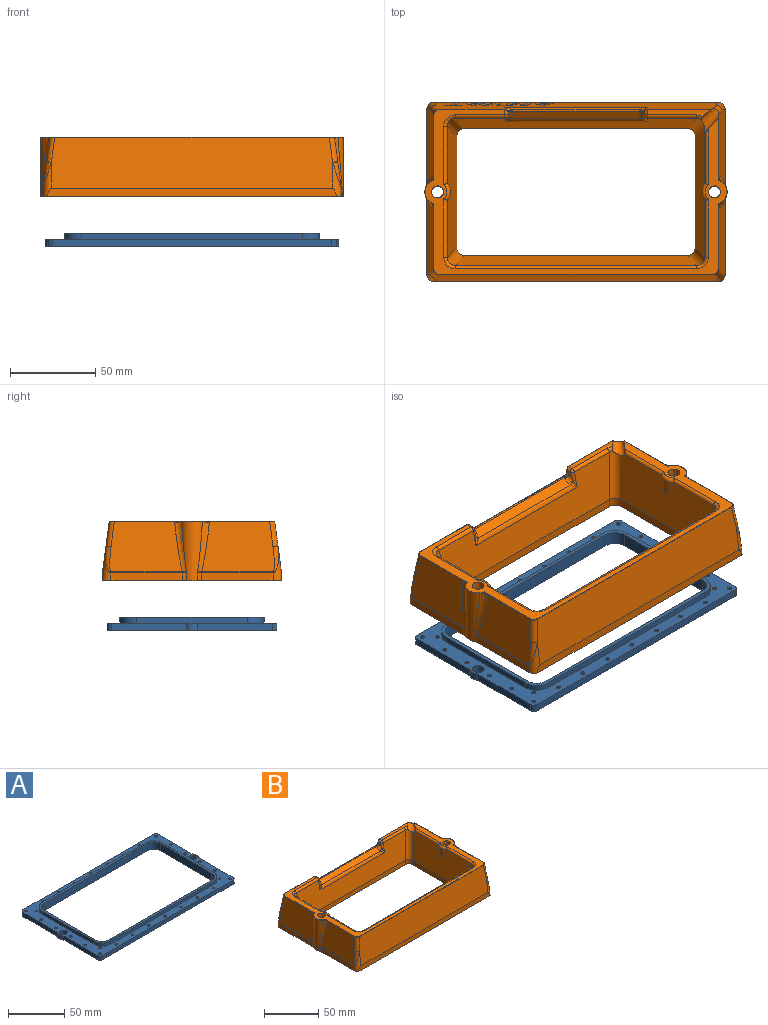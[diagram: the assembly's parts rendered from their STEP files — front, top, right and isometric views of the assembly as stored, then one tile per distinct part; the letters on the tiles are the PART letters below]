
ASSEMBLY  parts=2 mates=1
PART A: 104 faces, bbox 172.1x99.6x8 mm
  f0: plane 172.1x99.6mm, normal (0,0,-1), area 4703.2mm2, adj f3,f4,f5,f6,f7,f8,f9,f10
  f1: plane 172.1x99.6mm, normal (0,0,1), area 4007.9mm2, adj f3,f4,f5,f6,f7,f8,f9,f10
  f2: plane 149.6x84.6mm, normal (0,0,1), area 934.5mm2, adj f17,f18,f19,f20,f21,f22,f23,f24
  f3: plane 43.77x4.5mm, normal (1,0,0), area 197mm2, adj f0,f1,f4,f16
  f4: cylinder r=2.8mm len=4.5mm, axis (0,0,-1), area 19.8mm2, adj f0,f1,f3,f5
  f5: plane 164x4.5mm, normal (0,-1,0), area 738mm2, adj f0,f1,f4,f6
  f6: cylinder r=2.8mm len=4.5mm, axis (0,0,-1), area 19.8mm2, adj f0,f1,f5,f7
  f7: plane 43.77x4.5mm, normal (-1,0,0), area 197mm2, adj f0,f1,f6,f8
  f8: cylinder r=4.8mm len=6.46mm, axis (0,0,-1), area 31.9mm2, adj f0,f1,f7,f9
  f9: plane 43.77x4.5mm, normal (-1,0,0), area 197mm2, adj f0,f1,f8,f10
  f10: cylinder r=2.8mm len=4.5mm, axis (0,0,-1), area 19.8mm2, adj f0,f1,f9,f11
  f11: plane 164x4.5mm, normal (0,1,0), area 738mm2, adj f0,f1,f10,f12
  f12: cylinder r=2.8mm len=4.5mm, axis (0,0,-1), area 19.8mm2, adj f0,f1,f11,f13
  f13: plane 43.77x4.5mm, normal (1,0,0), area 197mm2, adj f0,f1,f12,f16
  f14: extruded ~6.97x6.97mm, area 99mm2, adj f0,f1
  f15: cylinder r=3.5mm len=7mm, axis (0,0,-1), area 99mm2, adj f0,f1
  f16: cylinder r=4.8mm len=6.46mm, axis (0,0,-1), area 31.9mm2, adj f0,f1,f3,f13
  f17: cylinder r=7.7mm len=8mm, axis (0,0,-1), area 96.8mm2, adj f0,f2,f18,f24
  f18: plane 65x8mm, normal (1,0,0), area 520mm2, adj f0,f2,f17,f19
  f19: cylinder r=7.7mm len=8mm, axis (0,0,-1), area 96.8mm2, adj f0,f2,f18,f20
  f20: plane 130x8mm, normal (0,-1,0), area 1040mm2, adj f0,f2,f19,f21
  f21: cylinder r=7.7mm len=8mm, axis (0,0,-1), area 96.8mm2, adj f0,f2,f20,f22
  f22: plane 65x8mm, normal (-1,0,0), area 520mm2, adj f0,f2,f21,f23
  f23: cylinder r=7.7mm len=8mm, axis (0,0,-1), area 96.8mm2, adj f0,f2,f22,f24
  f24: plane 130x8mm, normal (0,1,0), area 1040mm2, adj f0,f2,f17,f23
  f25: plane 65x0.5mm, normal (1,0,0), area 32.5mm2, adj f1,f26,f32,f41
  f26: cylinder r=10mm len=10mm, axis (0,0,1), area 7.9mm2, adj f1,f25,f27,f41
  f27: plane 130x0.5mm, normal (0,1,0), area 65mm2, adj f1,f26,f28,f41
  f28: cylinder r=10mm len=10mm, axis (0,0,1), area 7.9mm2, adj f1,f27,f29,f41
  f29: plane 65x0.5mm, normal (-1,0,0), area 32.5mm2, adj f1,f28,f30,f41
  f30: cylinder r=10mm len=10mm, axis (0,0,1), area 7.9mm2, adj f1,f29,f31,f41
  f31: plane 130x0.5mm, normal (0,-1,0), area 65mm2, adj f1,f30,f32,f41
  f32: cylinder r=10mm len=10mm, axis (0,0,1), area 7.9mm2, adj f1,f25,f31,f41
  f33: plane 65x4mm, normal (-1,0,0), area 260mm2, adj f2,f34,f40,f41
  f34: cylinder r=9.8mm len=9.8mm, axis (0,0,1), area 61.6mm2, adj f2,f33,f35,f41
  f35: plane 130x4mm, normal (0,1,0), area 520mm2, adj f2,f34,f36,f41
  f36: cylinder r=9.8mm len=9.8mm, axis (0,0,1), area 61.6mm2, adj f2,f35,f37,f41
  f37: plane 65x4mm, normal (1,0,0), area 260mm2, adj f2,f36,f38,f41
  f38: cylinder r=9.8mm len=9.8mm, axis (0,0,1), area 61.6mm2, adj f2,f37,f39,f41
  f39: plane 130x4mm, normal (0,-1,0), area 520mm2, adj f2,f38,f40,f41
  f40: cylinder r=9.8mm len=9.8mm, axis (0,0,1), area 61.6mm2, adj f2,f33,f39,f41
  f41: plane 150x85mm, normal (0,0,1), area 90.4mm2, adj f25,f26,f27,f28,f29,f30,f31,f32
  f42: cylinder r=1.25mm len=3.5mm, axis (0,0,-1), area 27.5mm2, adj f1,f91
  f43: cylinder r=1.25mm len=3.5mm, axis (0,0,-1), area 27.5mm2, adj f1,f77
  f44: cylinder r=1.25mm len=3.5mm, axis (0,0,-1), area 27.5mm2, adj f1,f75
  f45: cylinder r=1.25mm len=3.5mm, axis (0,0,-1), area 27.5mm2, adj f1,f74
  f46: cylinder r=1.25mm len=3.5mm, axis (0,0,-1), area 27.5mm2, adj f1,f73
  f47: cylinder r=1.25mm len=3.5mm, axis (0,0,-1), area 27.5mm2, adj f1,f89
  f48: cylinder r=1.25mm len=3.5mm, axis (0,0,-1), area 27.5mm2, adj f1,f88
  f49: cylinder r=1.25mm len=3.5mm, axis (0,0,-1), area 27.5mm2, adj f1,f87
  f50: cylinder r=1.25mm len=3.5mm, axis (0,0,-1), area 27.5mm2, adj f1,f102
  f51: cylinder r=1.25mm len=3.5mm, axis (0,0,-1), area 27.5mm2, adj f1,f76
  f52: cylinder r=1.25mm len=3.5mm, axis (0,0,-1), area 27.5mm2, adj f1,f86
  f53: cylinder r=1.25mm len=3.5mm, axis (0,0,-1), area 27.5mm2, adj f1,f92
  f54: cylinder r=1.25mm len=3.5mm, axis (0,0,-1), area 27.5mm2, adj f1,f103
  f55: cylinder r=1.25mm len=3.5mm, axis (0,0,-1), area 13.8mm2, adj f1,f56,f101
  f56: cylinder r=1.25mm len=3.5mm, axis (0,0,-1), area 13.8mm2, adj f1,f55,f100
  f57: cylinder r=1.25mm len=3.5mm, axis (0,0,-1), area 27.5mm2, adj f1,f83
  f58: cylinder r=1.25mm len=3.5mm, axis (0,0,-1), area 27.5mm2, adj f1,f95
  f59: cylinder r=1.25mm len=3.5mm, axis (0,0,-1), area 27.5mm2, adj f1,f82
  f60: cylinder r=1.25mm len=3.5mm, axis (0,0,-1), area 27.5mm2, adj f1,f96
  f61: cylinder r=1.25mm len=3.5mm, axis (0,0,-1), area 27.5mm2, adj f1,f85
  f62: cylinder r=1.25mm len=3.5mm, axis (0,0,-1), area 27.5mm2, adj f1,f93
  f63: cylinder r=1.25mm len=3.5mm, axis (0,0,-1), area 27.5mm2, adj f1,f84
  f64: cylinder r=1.25mm len=3.5mm, axis (0,0,-1), area 27.5mm2, adj f1,f94
  f65: cylinder r=1.25mm len=3.5mm, axis (0,0,-1), area 27.5mm2, adj f1,f79
  f66: cylinder r=1.25mm len=3.5mm, axis (0,0,-1), area 27.5mm2, adj f1,f99
  f67: cylinder r=1.25mm len=3.5mm, axis (0,0,-1), area 27.5mm2, adj f1,f78
  f68: cylinder r=1.25mm len=3.5mm, axis (0,0,-1), area 27.5mm2, adj f1,f90
  f69: cylinder r=1.25mm len=3.5mm, axis (0,0,-1), area 27.5mm2, adj f1,f81
  f70: cylinder r=1.25mm len=3.5mm, axis (0,0,-1), area 27.5mm2, adj f1,f97
  f71: cylinder r=1.25mm len=3.5mm, axis (0,0,-1), area 27.5mm2, adj f1,f80
  f72: cylinder r=1.25mm len=3.5mm, axis (0,0,-1), area 27.5mm2, adj f1,f98
  f73: cone r=1.25mm half-angle=45deg, axis (0,0,-1), area 15.6mm2, adj f0,f46
  f74: cone r=1.25mm half-angle=45deg, axis (0,0,-1), area 15.6mm2, adj f0,f45
  f75: cone r=1.25mm half-angle=45deg, axis (0,0,-1), area 15.6mm2, adj f0,f44
  f76: cone r=1.25mm half-angle=45deg, axis (0,0,-1), area 15.6mm2, adj f0,f51
  f77: cone r=1.25mm half-angle=45deg, axis (0,0,-1), area 15.6mm2, adj f0,f43
  f78: cone r=1.25mm half-angle=45deg, axis (0,0,-1), area 15.6mm2, adj f0,f67
  f79: cone r=1.25mm half-angle=45deg, axis (0,0,-1), area 15.6mm2, adj f0,f65
  f80: cone r=1.25mm half-angle=45deg, axis (0,0,-1), area 15.6mm2, adj f0,f71
  f81: cone r=1.25mm half-angle=45deg, axis (0,0,-1), area 15.6mm2, adj f0,f69
  f82: cone r=1.25mm half-angle=45deg, axis (0,0,-1), area 15.6mm2, adj f0,f59
  f83: cone r=1.25mm half-angle=45deg, axis (0,0,-1), area 15.6mm2, adj f0,f57
  f84: cone r=1.25mm half-angle=45deg, axis (0,0,-1), area 15.6mm2, adj f0,f63
  f85: cone r=1.25mm half-angle=45deg, axis (0,0,-1), area 15.6mm2, adj f0,f61
  f86: cone r=2.25mm half-angle=45deg, axis (0,0,-1), area 15.6mm2, adj f0,f52
  f87: cone r=1.25mm half-angle=45deg, axis (0,0,-1), area 15.6mm2, adj f0,f49
  f88: cone r=1.25mm half-angle=45deg, axis (0,0,-1), area 15.6mm2, adj f0,f48
  f89: cone r=1.25mm half-angle=45deg, axis (0,0,-1), area 15.6mm2, adj f0,f47
  f90: cone r=1.25mm half-angle=45deg, axis (0,0,-1), area 15.6mm2, adj f0,f68
  f91: cone r=1.25mm half-angle=45deg, axis (0,0,-1), area 15.6mm2, adj f0,f42
  f92: cone r=1.25mm half-angle=45deg, axis (0,0,-1), area 15.6mm2, adj f0,f53
  f93: cone r=1.25mm half-angle=45deg, axis (0,0,-1), area 15.6mm2, adj f0,f62
  f94: cone r=1.25mm half-angle=45deg, axis (0,0,-1), area 15.6mm2, adj f0,f64
  f95: cone r=1.25mm half-angle=45deg, axis (0,0,-1), area 15.6mm2, adj f0,f58
  f96: cone r=1.25mm half-angle=45deg, axis (0,0,-1), area 15.6mm2, adj f0,f60
  f97: cone r=1.25mm half-angle=45deg, axis (0,0,-1), area 15.6mm2, adj f0,f70
  f98: cone r=1.25mm half-angle=45deg, axis (0,0,-1), area 15.6mm2, adj f0,f72
  f99: cone r=1.25mm half-angle=45deg, axis (0,0,-1), area 15.6mm2, adj f0,f66
  f100: cone r=1.25mm half-angle=45deg, axis (0,0,-1), area 7.8mm2, adj f0,f56,f101
  f101: cone r=1.25mm half-angle=45deg, axis (0,0,-1), area 7.8mm2, adj f0,f55,f100
  f102: cone r=1.25mm half-angle=45deg, axis (0,0,-1), area 15.6mm2, adj f0,f50
  f103: cone r=2.25mm half-angle=45deg, axis (0,0,-1), area 15.6mm2, adj f0,f54
PART B: 310 faces, bbox 180.4x108x38.9 mm
  f0: plane 36.86x4.25mm, normal (0,0,1), area 113.1mm2, adj f1,f306,f307,f308,f309
  f1: bspline ~3.52x2.61mm, area 7.5mm2, adj f0,f2,f306,f309
  f2: cylinder r=5mm len=29.23mm, axis (0.19,0.19,0.96), area 222.6mm2, adj f1,f3,f304,f305,f309
  f3: plane 76.19x28.42mm, normal (-0.98,0,0.2), area 1980mm2, adj f2,f4,f298,f299,f300,f301,f302,f303
  f4: cylinder r=2mm len=32.81mm, axis (0,-1,0), area 86.4mm2, adj f3,f5,f299,f309
  f5: plane 177.35x96.9mm, normal (0,0,1), area 1738mm2, adj f4,f6,f268,f269,f270,f271,f272,f273
  f6: cylinder r=3.5mm len=30mm, axis (0,0,-1), area 659.7mm2, adj f5,f7
  f7: plane 172.5x100mm, normal (0,0,-1), area 4115.4mm2, adj f6,f8,f10,f12,f172,f173,f174,f175
  f8: cylinder r=1.25mm len=5mm, axis (0,0,-1), area 39.3mm2, adj f7,f9
  f9: plane 2.5x2.5mm, normal (0,0,-1), area 4.9mm2, adj f8
  f10: cylinder r=1.25mm len=5mm, axis (0,0,-1), area 39.3mm2, adj f7,f11
  f11: plane 2.5x2.5mm, normal (0,0,-1), area 4.9mm2, adj f10
  f12: cylinder r=5mm len=6.61mm, axis (0,0,-1), area 36.1mm2, adj f7,f13,f172,f182
  f13: plane 177.59x105.09mm, normal (0,0,-1), area 1373.2mm2, adj f12,f14,f36,f158,f159,f160,f161,f162
  f14: cylinder r=5mm len=4.67mm, axis (0,0,1), area 10.5mm2, adj f13,f15,f36,f171
  f15: bspline ~2.65x2.48mm, area 2.3mm2, adj f14,f16,f35,f36
  f16: bspline ~29.47x6.76mm, area 107.7mm2, adj f15,f17,f20,f36
  f17: bspline ~4.16x2.62mm, area 1.6mm2, adj f16,f18,f20,f273
  f18: bspline ~4.04x2.27mm, area 2.2mm2, adj f17,f19,f273,f276
  f19: bspline ~0.63x0.47mm, area 0mm2, adj f18,f274,f275
  f20: plane 44.36x31.16mm, normal (0.99,0,0.13), area 1161mm2, adj f16,f17,f21,f23,f35,f276
  f21: bspline ~15.36x4.97mm, area 46.2mm2, adj f20,f22,f23,f170
  f22: bspline ~1.14x1.07mm, area 0.1mm2, adj f21,f35,f170
  f23: cylinder r=3mm len=14.79mm, axis (0.13,-0.13,-0.98), area 69.4mm2, adj f20,f21,f24,f277
  f24: plane 165x29.83mm, normal (0,-0.99,0.13), area 4936.1mm2, adj f23,f25,f168,f169,f170,f278
  f25: cylinder r=3mm len=14.79mm, axis (-0.13,-0.13,-0.98), area 69.4mm2, adj f24,f26,f34,f279
  f26: bspline ~15.36x4.97mm, area 46.2mm2, adj f25,f27,f34,f168
  f27: bspline ~1.14x1.07mm, area 0.1mm2, adj f26,f28,f168
  f28: cylinder r=5mm len=42.28mm, axis (0,-1,0), area 27.9mm2, adj f27,f29,f34,f167
  f29: bspline ~2.48x2.36mm, area 2.3mm2, adj f28,f30,f165,f166
  f30: bspline ~29.47x6.76mm, area 107.7mm2, adj f29,f31,f34,f165
  f31: bspline ~4.16x2.62mm, area 1.6mm2, adj f30,f32,f34,f283
  f32: bspline ~4.04x2.27mm, area 2.2mm2, adj f31,f33,f280,f283
  f33: bspline ~0.63x0.47mm, area 0mm2, adj f32,f281,f282
  f34: plane 44.36x31.16mm, normal (-0.99,0,0.13), area 1161mm2, adj f25,f26,f28,f30,f31,f280
  f35: cylinder r=5mm len=42.28mm, axis (0,1,0), area 27.9mm2, adj f15,f20,f22,f171
  f36: cylinder r=7.5mm len=34.8mm, axis (0,0,1), area 355.5mm2, adj f13,f14,f15,f16,f37,f157,f158,f273
  f37: bspline ~29.47x6.76mm, area 107.7mm2, adj f36,f38,f154,f157
  f38: plane 44.36x31.16mm, normal (0.99,0,0.13), area 1159.1mm2, adj f37,f39,f151,f153,f154,f270,f309
  f39: cylinder r=3mm len=13.4mm, axis (-0.13,-0.13,0.98), area 62.3mm2, adj f38,f40,f151,f309
  f40: plane 165.16x29.99mm, normal (0,0.99,0.13), area 3946.1mm2, adj f39,f41,f50,f51,f52,f53,f54,f55
  f41: plane 2.79x0.99mm, normal (0,-0.13,0.99), area 2.8mm2, adj f40,f42,f50,f56
  f42: plane 13.68x12.08mm, normal (0,0.99,0.13), area 81.1mm2, adj f41,f43,f45,f46,f47,f48,f49,f50
  f43: extruded ~2.49x1.31mm, area 2.4mm2, adj f42,f44,f45,f49
  f44: plane 5.95x3.13mm, normal (0,0.99,0.13), area 8.9mm2, adj f43,f45,f46,f47,f48,f49
  f45: plane 1.04x0.47mm, normal (-1,0,0), area 0.3mm2, adj f42,f43,f44,f46
  f46: extruded ~2.5x1.31mm, area 2.6mm2, adj f42,f44,f45,f47
  f47: plane 3.72x1.77mm, normal (0.9,-0.06,0.43), area 4mm2, adj f42,f44,f46,f48
  f48: plane 3.13x0.99mm, normal (0,0.13,-0.99), area 3.1mm2, adj f42,f44,f47,f49
  f49: plane 3.39x1.43mm, normal (-1,-0.01,0.07), area 3.3mm2, adj f42,f43,f44,f48
  f50: plane 13.81x2.81mm, normal (1,0.01,-0.1), area 13.9mm2, adj f40,f41,f42,f51
  f51: plane 3.51x0.99mm, normal (0,0.13,-0.99), area 3.5mm2, adj f40,f42,f50,f52
  f52: plane 13.81x7.2mm, normal (-0.89,0.06,-0.46), area 15.6mm2, adj f40,f42,f51,f53
  f53: plane 3.01x0.99mm, normal (0,-0.13,0.99), area 3mm2, adj f40,f42,f52,f54
  f54: plane 3.38x1.62mm, normal (0.9,-0.06,0.44), area 3.6mm2, adj f40,f42,f53,f55
  f55: plane 4.44x0.99mm, normal (0,-0.13,0.99), area 4.4mm2, adj f40,f42,f54,f56
  f56: plane 3.38x1.42mm, normal (-1,-0.01,0.07), area 3.3mm2, adj f40,f41,f42,f55
  f57: extruded ~1.53x1.18mm, area 1.4mm2, adj f40,f58,f59,f68
  f58: plane 13.62x11.36mm, normal (0,0.99,0.13), area 70.5mm2, adj f57,f59,f60,f61,f62,f63,f64,f65
  f59: extruded ~1.37x1.16mm, area 1.3mm2, adj f40,f57,f58,f60
  f60: plane 8.33x2.08mm, normal (1,0.01,-0.06), area 8.3mm2, adj f40,f58,f59,f61
  f61: plane 2.77x0.99mm, normal (0,0.13,-0.99), area 2.8mm2, adj f40,f58,f60,f62
  f62: plane 13.75x2.81mm, normal (-1,-0.01,0.09), area 13.8mm2, adj f40,f58,f61,f63
  f63: plane 3.14x0.99mm, normal (0,-0.13,0.99), area 3.1mm2, adj f40,f58,f62,f64
  f64: plane 13.75x7.03mm, normal (0.89,-0.06,0.45), area 15.4mm2, adj f40,f58,f63,f65
  f65: plane 2.97x0.99mm, normal (0,0.13,-0.99), area 3mm2, adj f40,f58,f64,f66
  f66: plane 8.33x4.06mm, normal (-0.9,0.06,-0.44), area 9.2mm2, adj f40,f58,f65,f67
  f67: extruded ~2.77x1.34mm, area 2.9mm2, adj f40,f58,f66,f68
  f68: plane 0.99x0.13mm, normal (0,0.13,-0.99), area 0.1mm2, adj f40,f57,f58,f67
  f69: plane 10.31x2.35mm, normal (1,0.01,-0.06), area 10.3mm2, adj f40,f70,f71,f87
  f70: plane 16.53x13.62mm, normal (0,0.99,0.13), area 126.7mm2, adj f69,f71,f72,f73,f74,f75,f76,f77
  f71: plane 3.8x0.99mm, normal (0,0.13,-0.99), area 3.8mm2, adj f40,f69,f70,f72
  f72: plane 13.75x2.9mm, normal (-0.98,0.03,-0.2), area 14mm2, adj f40,f70,f71,f73
  f73: plane 2.58x0.99mm, normal (0,-0.13,0.99), area 2.6mm2, adj f40,f70,f72,f74
  f74: extruded ~8.54x2.11mm, area 8.7mm2, adj f40,f70,f73,f75
  f75: extruded ~2.28x1.28mm, area 2.2mm2, adj f40,f70,f74,f76
  f76: plane 0.99x0.13mm, normal (0,-0.13,0.99), area 0mm2, adj f40,f70,f75,f77
  f77: plane 10.69x2.4mm, normal (-1,-0.01,0.05), area 10.7mm2, adj f40,f70,f76,f78
  f78: plane 2.64x0.99mm, normal (0,-0.13,0.99), area 2.6mm2, adj f40,f70,f77,f79
  f79: plane 10.69x5.35mm, normal (0.89,-0.06,0.44), area 11.9mm2, adj f40,f70,f78,f80
  f80: plane 0.99x0.13mm, normal (0,-0.13,0.99), area 0mm2, adj f40,f70,f79,f81
  f81: extruded ~4.24x1.54mm, area 4.3mm2, adj f40,f70,f80,f82
  f82: plane 6.58x1.85mm, normal (-0.98,0.03,-0.2), area 6.6mm2, adj f40,f70,f81,f83
  f83: plane 2.63x0.99mm, normal (0,-0.13,0.99), area 2.6mm2, adj f40,f70,f82,f84
  f84: plane 13.75x2.91mm, normal (0.98,-0.03,0.21), area 14mm2, adj f40,f70,f83,f85
  f85: plane 3.98x0.99mm, normal (0,0.13,-0.99), area 4mm2, adj f40,f70,f84,f86
  f86: plane 10.31x5.18mm, normal (-0.89,0.06,-0.45), area 11.5mm2, adj f40,f70,f85,f87
  f87: plane 0.99x0.13mm, normal (0,0.13,-0.99), area 0mm2, adj f40,f69,f70,f86
  f88: plane 2.79x0.99mm, normal (0,-0.13,0.99), area 2.8mm2, adj f40,f89,f97,f103
  f89: plane 13.68x12.08mm, normal (0,0.99,0.13), area 81.1mm2, adj f88,f90,f92,f93,f94,f95,f96,f97
  f90: extruded ~2.49x1.31mm, area 2.4mm2, adj f89,f91,f92,f96
  f91: plane 5.95x3.13mm, normal (0,0.99,0.13), area 8.9mm2, adj f90,f92,f93,f94,f95,f96
  f92: plane 1.04x0.47mm, normal (-1,0,0), area 0.3mm2, adj f89,f90,f91,f93
  f93: extruded ~2.5x1.31mm, area 2.6mm2, adj f89,f91,f92,f94
  f94: plane 3.72x1.77mm, normal (0.9,-0.06,0.43), area 4mm2, adj f89,f91,f93,f95
  f95: plane 3.13x0.99mm, normal (0,0.13,-0.99), area 3.1mm2, adj f89,f91,f94,f96
  f96: plane 3.39x1.43mm, normal (-1,-0.01,0.07), area 3.3mm2, adj f89,f90,f91,f95
  f97: plane 13.81x2.81mm, normal (1,0.01,-0.1), area 13.9mm2, adj f40,f88,f89,f98
  f98: plane 3.51x0.99mm, normal (0,0.13,-0.99), area 3.5mm2, adj f40,f89,f97,f99
  f99: plane 13.81x7.2mm, normal (-0.89,0.06,-0.46), area 15.6mm2, adj f40,f89,f98,f100
  f100: plane 3.01x0.99mm, normal (0,-0.13,0.99), area 3mm2, adj f40,f89,f99,f101
  f101: plane 3.38x1.62mm, normal (0.9,-0.06,0.44), area 3.6mm2, adj f40,f89,f100,f102
  f102: plane 4.44x0.99mm, normal (0,-0.13,0.99), area 4.4mm2, adj f40,f89,f101,f103
  f103: plane 3.38x1.42mm, normal (-1,-0.01,0.07), area 3.3mm2, adj f40,f88,f89,f102
  f104: plane 3.32x0.99mm, normal (0,-0.13,0.99), area 3.3mm2, adj f40,f105,f106,f112
  f105: plane 13.62x10.01mm, normal (0,0.99,0.13), area 55.4mm2, adj f104,f106,f107,f108,f109,f110,f111,f112
  f106: plane 2.53x1.31mm, normal (0.98,-0.03,0.21), area 2.5mm2, adj f40,f104,f105,f107
  f107: plane 9.49x0.99mm, normal (0,0.13,-0.99), area 9.5mm2, adj f40,f105,f106,f108
  f108: plane 2.53x1.31mm, normal (-0.98,0.03,-0.21), area 2.5mm2, adj f40,f105,f107,f109
  f109: plane 3.31x0.99mm, normal (0,-0.13,0.99), area 3.3mm2, adj f40,f105,f108,f110
  f110: plane 11.35x2.49mm, normal (-0.98,0.03,-0.2), area 11.6mm2, adj f40,f105,f109,f111
  f111: plane 2.87x0.99mm, normal (0,-0.13,0.99), area 2.9mm2, adj f40,f105,f110,f112
  f112: plane 11.35x2.49mm, normal (0.98,-0.03,0.2), area 11.6mm2, adj f40,f104,f105,f111
  f113: cylinder r=2mm len=6.83mm, axis (0,-0.13,0.99), area 9.1mm2, adj f40,f114,f115,f134,f135,f136
  f114: bspline ~2.28x2mm, area 0.4mm2, adj f113,f307,f308
  f115: plane 1.89x1.26mm, normal (-1,0,0), area 1mm2, adj f113,f116,f132,f133,f307
  f116: cylinder r=2mm len=10.44mm, axis (0,0.2,0.98), area 18mm2, adj f115,f117,f118,f131,f304
  f117: sphere r=2mm, area 5.7mm2, adj f116,f306,f307
  f118: bspline ~5.1x4.05mm, area 5.1mm2, adj f116,f119,f131
  f119: cylinder r=5mm len=84mm, axis (1,0,0), area 275.2mm2, adj f118,f120,f130,f304
  f120: bspline ~5.1x4.05mm, area 5.1mm2, adj f119,f121,f129
  f121: cylinder r=2mm len=10.44mm, axis (0,-0.2,-0.98), area 18mm2, adj f120,f122,f123,f129,f304
  f122: sphere r=2mm, area 7.8mm2, adj f121,f289,f290
  f123: plane 1.89x1.26mm, normal (1,0,0), area 1mm2, adj f121,f124,f128,f139,f289
  f124: torus R=4mm, axis (1,0,0), area 4.3mm2, adj f123,f125,f126,f128
  f125: cylinder r=1mm len=75.23mm, axis (1,0,0), area 78.5mm2, adj f124,f126,f130,f133,f134,f137
  f126: bspline ~3.46x3.12mm, area 2.5mm2, adj f124,f125,f127,f139
  f127: bspline ~3.6x3.45mm, area 2.8mm2, adj f126,f137,f139
  f128: cylinder r=3mm len=3mm, axis (0,-0.77,-0.63), area 2.1mm2, adj f123,f124,f129,f130
  f129: bspline ~6.98x5.56mm, area 17.3mm2, adj f120,f121,f128,f130
  f130: plane 76.29x4.24mm, normal (0,-0.63,0.77), area 409.4mm2, adj f119,f125,f128,f129,f131,f132
  f131: bspline ~6.98x5.56mm, area 17.3mm2, adj f116,f118,f130,f132
  f132: cylinder r=3mm len=3mm, axis (0,-0.77,-0.63), area 2.1mm2, adj f115,f130,f131,f133
  f133: torus R=4mm, axis (1,0,0), area 4.3mm2, adj f115,f125,f132,f134
  f134: bspline ~3.46x3.12mm, area 2.5mm2, adj f113,f125,f133,f135
  f135: bspline ~3.6x3.45mm, area 2.8mm2, adj f113,f134,f137
  f136: bspline ~2.91x2.84mm, area 0.9mm2, adj f113,f137
  f137: cylinder r=2mm len=84mm, axis (1,0,0), area 170.4mm2, adj f40,f125,f127,f135,f136,f138
  f138: bspline ~2.91x2.84mm, area 0.9mm2, adj f137,f139
  f139: cylinder r=2mm len=6.83mm, axis (0,0.13,-0.99), area 9.1mm2, adj f40,f123,f126,f127,f138,f140
  f140: bspline ~2.28x2mm, area 0.4mm2, adj f139,f288,f289
  f141: cylinder r=3mm len=14.79mm, axis (0.13,-0.13,0.98), area 69.4mm2, adj f40,f142,f150,f287
  f142: plane 44.36x31.16mm, normal (-0.99,0,0.13), area 1161mm2, adj f141,f143,f146,f149,f150,f286
  f143: cylinder r=5mm len=42.28mm, axis (0,-1,0), area 27.9mm2, adj f142,f144,f145,f163
  f144: bspline ~2.65x2.48mm, area 2.3mm2, adj f143,f149,f164,f165
  f145: bspline ~1.14x1.07mm, area 0.1mm2, adj f143,f150,f162
  f146: bspline ~4.16x2.62mm, area 1.6mm2, adj f142,f147,f149,f283
  f147: bspline ~4.04x2.27mm, area 2.2mm2, adj f146,f148,f283,f286
  f148: bspline ~0.63x0.47mm, area 0mm2, adj f147,f284,f285
  f149: bspline ~29.47x6.76mm, area 107.7mm2, adj f142,f144,f146,f165
  f150: bspline ~15.36x4.97mm, area 46.2mm2, adj f141,f142,f145,f162
  f151: bspline ~15.36x4.97mm, area 46.2mm2, adj f38,f39,f152,f160
  f152: bspline ~1.14x1.07mm, area 0.1mm2, adj f151,f153,f160
  f153: cylinder r=5mm len=42.28mm, axis (0,1,0), area 27.9mm2, adj f38,f152,f157,f159
  f154: bspline ~4.16x2.62mm, area 1.6mm2, adj f37,f38,f155,f273
  f155: bspline ~4.04x2.27mm, area 2.2mm2, adj f154,f156,f270,f273
  f156: bspline ~0.63x0.47mm, area 0mm2, adj f155,f271,f272
  f157: bspline ~2.48x2.36mm, area 2.3mm2, adj f36,f37,f153,f158
  f158: cylinder r=5mm len=4.67mm, axis (0,0,1), area 10.5mm2, adj f13,f36,f157,f159
  f159: plane 42.67x4.67mm, normal (1,0,0), area 197.8mm2, adj f13,f153,f158,f160
  f160: cylinder r=5mm len=20.77mm, axis (0,0.13,-0.99), area 74.3mm2, adj f13,f40,f151,f152,f159,f161
  f161: plane 169.97x5mm, normal (0,1,0), area 841.8mm2, adj f13,f40,f160,f162
  f162: cylinder r=5mm len=20.77mm, axis (0,-0.13,0.99), area 74.3mm2, adj f13,f40,f145,f150,f161,f163
  f163: plane 42.67x4.67mm, normal (-1,0,0), area 197.8mm2, adj f13,f143,f162,f164
  f164: cylinder r=5mm len=4.67mm, axis (0,0,1), area 10.5mm2, adj f13,f144,f163,f165
  f165: cylinder r=7.5mm len=34.8mm, axis (0,0,1), area 355.5mm2, adj f13,f29,f30,f144,f149,f164,f166,f283
  f166: cylinder r=5mm len=4.67mm, axis (0,0,1), area 10.5mm2, adj f13,f29,f165,f167
  f167: plane 42.67x4.67mm, normal (-1,0,0), area 197.8mm2, adj f13,f28,f166,f168
  f168: cylinder r=5mm len=20.77mm, axis (0,-0.13,-0.99), area 74.3mm2, adj f13,f24,f26,f27,f167,f169
  f169: plane 169.97x5mm, normal (0,-1,0), area 841.8mm2, adj f13,f24,f168,f170
  f170: cylinder r=5mm len=20.77mm, axis (0,0.13,0.99), area 74.3mm2, adj f13,f21,f22,f24,f169,f171
  f171: plane 42.67x4.67mm, normal (1,0,0), area 197.8mm2, adj f13,f14,f35,f170
  f172: plane 43.69x5mm, normal (-1,0,0), area 218.5mm2, adj f7,f12,f13,f173
  f173: cylinder r=3mm len=5mm, axis (0,0,-1), area 23.6mm2, adj f7,f13,f172,f174
  f174: plane 164x5mm, normal (0,-1,0), area 820mm2, adj f7,f13,f173,f175
  f175: cylinder r=3mm len=5mm, axis (0,0,1), area 23.6mm2, adj f7,f13,f174,f176
  f176: plane 43.69x5mm, normal (1,0,0), area 218.5mm2, adj f7,f13,f175,f177
  f177: cylinder r=5mm len=6.61mm, axis (0,0,-1), area 36.1mm2, adj f7,f13,f176,f178
  f178: plane 43.69x5mm, normal (1,0,0), area 218.5mm2, adj f7,f13,f177,f179
  f179: cylinder r=3mm len=5mm, axis (0,0,-1), area 23.6mm2, adj f7,f13,f178,f180
  f180: plane 164x5mm, normal (0,1,0), area 820mm2, adj f7,f13,f179,f181
  f181: cylinder r=3mm len=5mm, axis (0,0,1), area 23.6mm2, adj f7,f13,f180,f182
  f182: plane 43.69x5mm, normal (-1,0,0), area 218.5mm2, adj f7,f12,f13,f181
  f183: cylinder r=10mm len=10mm, axis (0,0,-1), area 55mm2, adj f7,f184,f204,f210
  f184: plane 150x85mm, normal (0,0,-1), area 1112.4mm2, adj f183,f185,f197,f198,f199,f200,f201,f202
  f185: cylinder r=7.5mm len=8.5mm, axis (0,0,-1), area 100.1mm2, adj f184,f186,f197,f203
  f186: plane 145x80mm, normal (0,0,-1), area 1073.2mm2, adj f185,f187,f193,f194,f195,f196,f197,f198
  f187: plane 130x5mm, normal (0,1,0), area 650mm2, adj f186,f188,f193,f302
  f188: plane 141.55x28.4mm, normal (0,0.98,0.2), area 3934.1mm2, adj f187,f189,f193,f296,f301,f302
  f189: cylinder r=5mm len=28.78mm, axis (0.19,0.19,-0.96), area 226.1mm2, adj f188,f190,f193,f295
  f190: plane 76.57x28.42mm, normal (0.98,0,0.2), area 1984.4mm2, adj f189,f191,f192,f193,f194,f195,f292,f293
  f191: cylinder r=7.5mm len=9.86mm, axis (0,0,1), area 65.8mm2, adj f190,f293
  f192: cylinder r=5mm len=28.78mm, axis (-0.19,0.19,0.96), area 226.1mm2, adj f190,f195,f291,f304
  f193: cylinder r=5mm len=5mm, axis (0,0,-1), area 38.3mm2, adj f186,f187,f188,f189,f190,f194
  f194: plane 65x5mm, normal (1,0,0), area 325mm2, adj f186,f190,f193,f195
  f195: cylinder r=5mm len=5mm, axis (0,0,1), area 38.3mm2, adj f186,f190,f192,f194,f196,f304
  f196: plane 130x5mm, normal (0,-1,0), area 650mm2, adj f186,f195,f304,f305
  f197: plane 65x8.5mm, normal (-1,0,0), area 552.5mm2, adj f184,f185,f186,f198
  f198: cylinder r=7.5mm len=8.5mm, axis (0,0,-1), area 100.1mm2, adj f184,f186,f197,f199
  f199: plane 130x8.5mm, normal (0,1,0), area 1105mm2, adj f184,f186,f198,f200
  f200: cylinder r=7.5mm len=8.5mm, axis (0,0,-1), area 100.1mm2, adj f184,f186,f199,f201
  f201: plane 65x8.5mm, normal (1,0,0), area 552.5mm2, adj f184,f186,f200,f202
  f202: cylinder r=7.5mm len=8.5mm, axis (0,0,-1), area 100.1mm2, adj f184,f186,f201,f203
  f203: plane 130x8.5mm, normal (0,-1,0), area 1105mm2, adj f184,f185,f186,f202
  f204: plane 130x3.5mm, normal (0,-1,0), area 455mm2, adj f7,f183,f184,f205
  f205: cylinder r=10mm len=10mm, axis (0,0,-1), area 55mm2, adj f7,f184,f204,f206
  f206: plane 65x3.5mm, normal (-1,0,0), area 227.5mm2, adj f7,f184,f205,f207
  f207: cylinder r=10mm len=10mm, axis (0,0,-1), area 55mm2, adj f7,f184,f206,f208
  f208: plane 130x3.5mm, normal (0,1,0), area 455mm2, adj f7,f184,f207,f209
  f209: cylinder r=10mm len=10mm, axis (0,0,-1), area 55mm2, adj f7,f184,f208,f210
  f210: plane 65x3.5mm, normal (1,0,0), area 227.5mm2, adj f7,f183,f184,f209
  f211: cylinder r=1.25mm len=5mm, axis (0,0,-1), area 39.3mm2, adj f7,f212
  f212: plane 2.5x2.5mm, normal (0,0,-1), area 4.9mm2, adj f211
  f213: cylinder r=1.25mm len=5mm, axis (0,0,-1), area 39.3mm2, adj f7,f214
  f214: plane 2.5x2.5mm, normal (0,0,-1), area 4.9mm2, adj f213
  f215: cylinder r=1.25mm len=5mm, axis (0,0,-1), area 39.3mm2, adj f7,f216
  f216: plane 2.5x2.5mm, normal (0,0,-1), area 4.9mm2, adj f215
  f217: cylinder r=1.25mm len=5mm, axis (0,0,-1), area 39.3mm2, adj f7,f218
  f218: plane 2.5x2.5mm, normal (0,0,-1), area 4.9mm2, adj f217
  f219: cylinder r=1.25mm len=5mm, axis (0,0,-1), area 39.3mm2, adj f7,f220
  f220: plane 2.5x2.5mm, normal (0,0,-1), area 4.9mm2, adj f219
  f221: cylinder r=1.25mm len=5mm, axis (0,0,-1), area 39.3mm2, adj f7,f222
  f222: plane 2.5x2.5mm, normal (0,0,-1), area 4.9mm2, adj f221
  f223: cylinder r=1.25mm len=5mm, axis (0,0,-1), area 39.3mm2, adj f7,f224
  f224: plane 2.5x2.5mm, normal (0,0,-1), area 4.9mm2, adj f223
  f225: cylinder r=1.25mm len=5mm, axis (0,0,-1), area 39.3mm2, adj f7,f226
  f226: plane 2.5x2.5mm, normal (0,0,-1), area 4.9mm2, adj f225
  f227: cylinder r=1.25mm len=5mm, axis (0,0,-1), area 39.3mm2, adj f7,f228
  f228: plane 2.5x2.5mm, normal (0,0,-1), area 4.9mm2, adj f227
  f229: cylinder r=1.25mm len=5mm, axis (0,0,-1), area 39.3mm2, adj f7,f230
  f230: plane 2.5x2.5mm, normal (0,0,-1), area 4.9mm2, adj f229
  f231: cylinder r=1.25mm len=5mm, axis (0,0,-1), area 39.3mm2, adj f7,f232
  f232: plane 2.5x2.5mm, normal (0,0,-1), area 4.9mm2, adj f231
  f233: cylinder r=1.25mm len=5mm, axis (0,0,-1), area 19.7mm2, adj f7,f234,f235
  f234: plane 2.52x2.5mm, normal (0,0,-1), area 5mm2, adj f233,f235
  f235: cylinder r=1.25mm len=5mm, axis (0,0,-1), area 19.7mm2, adj f7,f233,f234
  f236: cylinder r=1.25mm len=5mm, axis (0,0,-1), area 39.3mm2, adj f7,f237
  f237: plane 2.5x2.5mm, normal (0,0,-1), area 4.9mm2, adj f236
  f238: cylinder r=1.25mm len=5mm, axis (0,0,-1), area 39.3mm2, adj f7,f239
  f239: plane 2.5x2.5mm, normal (0,0,-1), area 4.9mm2, adj f238
  f240: cylinder r=1.25mm len=5mm, axis (0,0,-1), area 39.3mm2, adj f7,f241
  f241: plane 2.5x2.5mm, normal (0,0,-1), area 4.9mm2, adj f240
  f242: cylinder r=1.25mm len=5mm, axis (0,0,-1), area 39.3mm2, adj f7,f243
  f243: plane 2.5x2.5mm, normal (0,0,-1), area 4.9mm2, adj f242
  f244: cylinder r=1.25mm len=5mm, axis (0,0,-1), area 39.3mm2, adj f7,f245
  f245: plane 2.5x2.5mm, normal (0,0,-1), area 4.9mm2, adj f244
  f246: cylinder r=1.25mm len=5mm, axis (0,0,-1), area 39.3mm2, adj f7,f247
  f247: plane 2.5x2.5mm, normal (0,0,-1), area 4.9mm2, adj f246
  f248: cylinder r=1.25mm len=5mm, axis (0,0,-1), area 39.3mm2, adj f7,f249
  f249: plane 2.5x2.5mm, normal (0,0,-1), area 4.9mm2, adj f248
  f250: cylinder r=1.25mm len=5mm, axis (0,0,-1), area 39.3mm2, adj f7,f251
  f251: plane 2.5x2.5mm, normal (0,0,-1), area 4.9mm2, adj f250
  f252: cylinder r=1.25mm len=5mm, axis (0,0,-1), area 39.3mm2, adj f7,f253
  f253: plane 2.5x2.5mm, normal (0,0,-1), area 4.9mm2, adj f252
  f254: cylinder r=1.25mm len=5mm, axis (0,0,-1), area 39.3mm2, adj f7,f255
  f255: plane 2.5x2.5mm, normal (0,0,-1), area 4.9mm2, adj f254
  f256: cylinder r=1.25mm len=5mm, axis (0,0,-1), area 39.3mm2, adj f7,f257
  f257: plane 2.5x2.5mm, normal (0,0,-1), area 4.9mm2, adj f256
  f258: cylinder r=1.25mm len=5mm, axis (0,0,-1), area 39.3mm2, adj f7,f259
  f259: plane 2.5x2.5mm, normal (0,0,-1), area 4.9mm2, adj f258
  f260: cylinder r=1.25mm len=5mm, axis (0,0,-1), area 39.3mm2, adj f7,f261
  f261: plane 2.5x2.5mm, normal (0,0,-1), area 4.9mm2, adj f260
  f262: cylinder r=1.25mm len=5mm, axis (0,0,-1), area 39.3mm2, adj f7,f263
  f263: plane 2.5x2.5mm, normal (0,0,-1), area 4.9mm2, adj f262
  f264: cylinder r=1.25mm len=5mm, axis (0,0,-1), area 39.3mm2, adj f7,f265
  f265: plane 2.5x2.5mm, normal (0,0,-1), area 4.9mm2, adj f264
  f266: cylinder r=1.25mm len=5mm, axis (0,0,-1), area 39.3mm2, adj f7,f267
  f267: plane 2.5x2.5mm, normal (0,0,-1), area 4.9mm2, adj f266
  f268: cylinder r=3.5mm len=30mm, axis (0,0,-1), area 622.1mm2, adj f5,f7,f269
  f269: extruded ~9.4x5.36mm, area 37.7mm2, adj f5,f268
  f270: cylinder r=0.2mm len=36.54mm, axis (0,-1,0), area 9.9mm2, adj f5,f38,f155,f309
  f271: cylinder r=0.2mm len=0.12mm, axis (0,-1,0), area 0mm2, adj f5,f156
  f272: torus R=7.3mm, axis (0,0,1), area 0mm2, adj f5,f156
  f273: torus R=7.3mm, axis (0,0,1), area 4.8mm2, adj f5,f17,f18,f36,f154,f155
  f274: torus R=7.3mm, axis (0,0,1), area 0mm2, adj f5,f19
  f275: cylinder r=0.2mm len=0.13mm, axis (0,-1,0), area 0mm2, adj f5,f19
  f276: cylinder r=0.2mm len=38.42mm, axis (0,-1,0), area 10.5mm2, adj f5,f18,f20,f277
  f277: bspline ~2.97x2.97mm, area 1.3mm2, adj f5,f23,f276,f278
  f278: cylinder r=0.2mm len=161.1mm, axis (-1,0,0), area 46.3mm2, adj f5,f24,f277,f279
  f279: bspline ~2.97x2.97mm, area 1.3mm2, adj f5,f25,f278,f280
  f280: cylinder r=0.2mm len=38.43mm, axis (0,-1,0), area 10.5mm2, adj f5,f32,f34,f279
  f281: cylinder r=0.2mm len=0.12mm, axis (0,-1,0), area 0mm2, adj f5,f33
  f282: torus R=7.3mm, axis (0,0,1), area 0mm2, adj f5,f33
  f283: torus R=7.3mm, axis (0,0,1), area 4.8mm2, adj f5,f31,f32,f146,f147,f165
  f284: torus R=7.3mm, axis (0,0,1), area 0mm2, adj f5,f148
  f285: cylinder r=0.2mm len=0.13mm, axis (0,-1,0), area 0mm2, adj f5,f148
  f286: cylinder r=0.2mm len=38.42mm, axis (0,-1,0), area 10.5mm2, adj f5,f142,f147,f287
  f287: bspline ~3.13x3.13mm, area 1.3mm2, adj f5,f141,f286,f288
  f288: cylinder r=0.2mm len=38.55mm, axis (-1,0,0), area 11.1mm2, adj f5,f40,f140,f287
  f289: cylinder r=2mm len=3.19mm, axis (0,1,0), area 7.5mm2, adj f5,f122,f123,f140
  f290: cylinder r=2mm len=28.78mm, axis (-1,0,0), area 79mm2, adj f5,f122,f291,f304
  f291: bspline ~6.86x6.86mm, area 23.8mm2, adj f5,f192,f290,f292
  f292: cylinder r=2mm len=34.13mm, axis (0,-1,0), area 92.6mm2, adj f5,f190,f291,f293
  f293: torus R=5.5mm, axis (0,0,1), area 33.1mm2, adj f5,f190,f191,f292,f294
  f294: cylinder r=2mm len=34.13mm, axis (0,-1,0), area 92.6mm2, adj f5,f190,f293,f295
  f295: bspline ~6.86x6.86mm, area 23.8mm2, adj f5,f189,f294,f296
  f296: cylinder r=2mm len=141.55mm, axis (-1,0,0), area 388.8mm2, adj f5,f188,f295,f297
  f297: bspline ~6.86x6.86mm, area 23.8mm2, adj f5,f296,f300,f301
  f298: cylinder r=7.5mm len=9.86mm, axis (0,0,1), area 65.8mm2, adj f3,f299
  f299: torus R=5.5mm, axis (0,0,1), area 33.1mm2, adj f3,f4,f5,f298,f300
  f300: cylinder r=2mm len=34.13mm, axis (0,-1,0), area 92.6mm2, adj f3,f5,f297,f299
  f301: cylinder r=5mm len=28.78mm, axis (-0.19,0.19,-0.96), area 226.1mm2, adj f3,f188,f297,f302
  f302: cylinder r=5mm len=5mm, axis (0,0,1), area 38.3mm2, adj f3,f186,f187,f188,f301,f303
  f303: plane 65x5mm, normal (-1,0,0), area 325mm2, adj f3,f186,f302,f305
  f304: plane 141.55x28.4mm, normal (0,-0.98,0.2), area 3073.4mm2, adj f2,f116,f119,f121,f192,f195,f196,f290
  f305: cylinder r=5mm len=5mm, axis (0,0,-1), area 38.3mm2, adj f2,f3,f186,f196,f303,f304
  f306: cylinder r=2mm len=28.78mm, axis (-1,0,0), area 79mm2, adj f0,f1,f117,f304
  f307: cylinder r=2mm len=3.19mm, axis (0,-1,0), area 7.5mm2, adj f0,f114,f115,f117
  f308: cylinder r=0.2mm len=37.03mm, axis (-1,0,0), area 10.6mm2, adj f0,f40,f114,f309
  f309: bspline ~15.39x15.07mm, area 112.6mm2, adj f0,f1,f2,f3,f4,f5,f38,f39
PLACE A t=(15.63,2.73,58.38)mm
PLACE B rot(axis=(0.3,0.93,-0.22),0deg) t=(15.63,2.73,57.88)mm
MATE parallel A.f1 <-> B.f7  axis (0,0,1) through (15.63,2.73,32.88)mm
